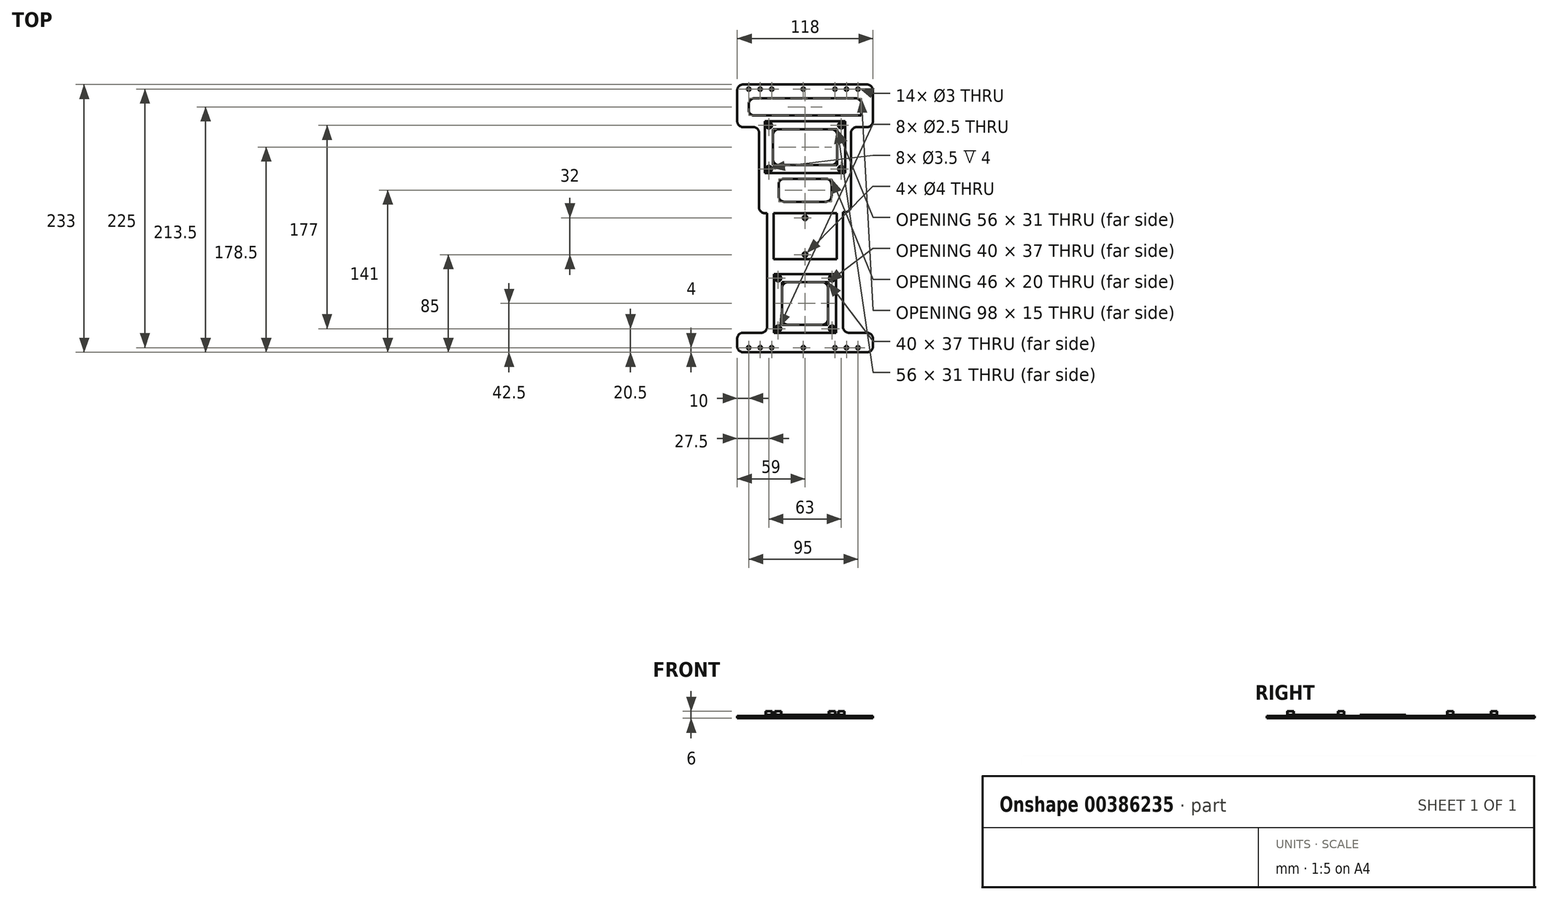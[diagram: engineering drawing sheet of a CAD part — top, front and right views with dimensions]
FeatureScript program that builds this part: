
annotation { "Feature Type Name" : "Feature", "Feature Type Description" : "" }
export const myFeature = defineFeature(function(context is Context, id is Id, definition is map)
    precondition{}
    {
        {
            var Q0;
            Q0=qCreatedBy(makeId("Top.planeOp"),FACE);
            var sketch = newSketch(context, id + "F0", { "sketchPlane" : qUnion([Q0])});
            skLineSegment(sketch, "E0.bottom", {"start": v(-25.5, -34.75) * mm, "end": v(28.5, -34.75) * mm});
            skLineSegment(sketch, "E0.top", {"start": v(-25.5, -85.75) * mm, "end": v(28.5, -85.75) * mm});
            skLineSegment(sketch, "E0.left", {"start": v(-25.5, -34.75) * mm, "end": v(-25.5, -85.75) * mm});
            skLineSegment(sketch, "E0.right", {"start": v(28.5, -34.75) * mm, "end": v(28.5, -85.75) * mm});
            skCircle(sketch, "E1", {"center": v(-22, -38.25) * mm, "radius": 1.75 * mm});
            skCircle(sketch, "E2", {"center": v(-22, -82.25) * mm, "radius": 1.75 * mm});
            skCircle(sketch, "E3", {"center": v(25, -82.25) * mm, "radius": 1.75 * mm});
            skCircle(sketch, "E4", {"center": v(25, -38.25) * mm, "radius": 1.75 * mm});
            skLineSegment(sketch, "E5.bottom", {"start": v(-18.5, -78.75) * mm, "end": v(21.5, -78.75) * mm});
            skLineSegment(sketch, "E5.top", {"start": v(-18.5, -41.75) * mm, "end": v(21.5, -41.75) * mm});
            skLineSegment(sketch, "E5.left", {"start": v(-18.5, -78.75) * mm, "end": v(-18.5, -41.75) * mm});
            skLineSegment(sketch, "E5.right", {"start": v(21.5, -78.75) * mm, "end": v(21.5, -41.75) * mm});
            skCircle(sketch, "E6", {"center": v(-22, -38.25) * mm, "radius": 2.75 * mm});
            skCircle(sketch, "E7", {"center": v(-22, -82.25) * mm, "radius": 2.75 * mm});
            skCircle(sketch, "E8", {"center": v(25, -82.25) * mm, "radius": 2.75 * mm});
            skCircle(sketch, "E9", {"center": v(25, -38.25) * mm, "radius": 2.75 * mm});
            skSolve(sketch);
        }
        {
            var Q0;
            Q0=makeQuery(id+"F0.imprint","IMPRINT",FACE,{"disambiguationData":[TD([[makeQuery(id+"F0.imprint","IMPRINT",EDGE,{"derivedFrom":sQuery(id+"F0.wireOp",EDGE,"E0.bottom")}),-1.0]])]});
            extrude(context, id + "F1", {"entities" : qUnion([Q0]), "depth" : 1 * mm});
        }
        {
            var Q0;
            Q0=makeQuery(id+"F0.imprint","IMPRINT",FACE,{"disambiguationData":[TD([[makeQuery(id+"F0.imprint","IMPRINT",EDGE,{"derivedFrom":sQuery(id+"F0.wireOp",EDGE,"E1")}),-1.0]])]});
            var Q1;
            Q1=makeQuery(id+"F0.imprint","IMPRINT",FACE,{"disambiguationData":[TD([[makeQuery(id+"F0.imprint","IMPRINT",EDGE,{"derivedFrom":sQuery(id+"F0.wireOp",EDGE,"E4")}),-1.0]])]});
            var Q2;
            Q2=makeQuery(id+"F0.imprint","IMPRINT",FACE,{"disambiguationData":[TD([[makeQuery(id+"F0.imprint","IMPRINT",EDGE,{"derivedFrom":sQuery(id+"F0.wireOp",EDGE,"E3")}),-1.0]])]});
            var Q3;
            Q3=makeQuery(id+"F0.imprint","IMPRINT",FACE,{"disambiguationData":[TD([[makeQuery(id+"F0.imprint","IMPRINT",EDGE,{"derivedFrom":sQuery(id+"F0.wireOp",EDGE,"E2")}),-1.0]])]});
            extrude(context, id + "F2", {"entities" : qUnion([Q0, Q1, Q2, Q3]), "operationType" : NewBodyOperationType.ADD, "depth" : 4 * mm});
        }
        {
            var Q0;
            Q0=qCreatedBy(makeId("Top.planeOp"),FACE);
            var sketch = newSketch(context, id + "F3", { "sketchPlane" : qUnion([Q0])});
            skLineSegment(sketch, "E10.bottom", {"start": v(-26, 18.25) * mm, "end": v(29, 18.25) * mm});
            skLineSegment(sketch, "E10.top", {"start": v(-26, -21.75) * mm, "end": v(29, -21.75) * mm});
            skLineSegment(sketch, "E10.left", {"start": v(-26, 18.25) * mm, "end": v(-26, -21.75) * mm});
            skLineSegment(sketch, "E10.right", {"start": v(29, 18.25) * mm, "end": v(29, -21.75) * mm});
            skCircle(sketch, "E11", {"center": v(1.5, 14.25) * mm, "radius": 2 * mm});
            skCircle(sketch, "E12", {"center": v(1.5, -17.75) * mm, "radius": 2 * mm});
            skSolve(sketch);
        }
        {
            var Q0;
            Q0 = qSketchRegion(id + "F3", true);
            extrude(context, id + "F4", {"entities" : qUnion([Q0]), "depth" : 1 * mm});
        }
        {
            var Q0;
            Q0=qCreatedBy(makeId("Top.planeOp"),FACE);
            var sketch = newSketch(context, id + "F5", { "sketchPlane" : qUnion([Q0])});
            skLineSegment(sketch, "E13.bottom", {"start": v(-33.5, 98.25) * mm, "end": v(36.5, 98.25) * mm});
            skLineSegment(sketch, "E13.top", {"start": v(-33.5, 53.25) * mm, "end": v(36.5, 53.25) * mm});
            skLineSegment(sketch, "E13.left", {"start": v(-33.5, 98.25) * mm, "end": v(-33.5, 53.25) * mm});
            skLineSegment(sketch, "E13.right", {"start": v(36.5, 98.25) * mm, "end": v(36.5, 53.25) * mm});
            skCircle(sketch, "E14", {"center": v(-30, 94.75) * mm, "radius": 1.75 * mm});
            skCircle(sketch, "E15", {"center": v(-30, 56.75) * mm, "radius": 1.75 * mm});
            skCircle(sketch, "E16", {"center": v(33, 56.75) * mm, "radius": 1.75 * mm});
            skCircle(sketch, "E17", {"center": v(33, 94.75) * mm, "radius": 1.75 * mm});
            skLineSegment(sketch, "E18.bottom", {"start": v(-26.5, 60.25) * mm, "end": v(29.5, 60.25) * mm});
            skLineSegment(sketch, "E18.top", {"start": v(-26.5, 91.25) * mm, "end": v(29.5, 91.25) * mm});
            skLineSegment(sketch, "E18.left", {"start": v(-26.5, 60.25) * mm, "end": v(-26.5, 91.25) * mm});
            skLineSegment(sketch, "E18.right", {"start": v(29.5, 60.25) * mm, "end": v(29.5, 91.25) * mm});
            skCircle(sketch, "E19", {"center": v(-30, 94.75) * mm, "radius": 2.75 * mm});
            skCircle(sketch, "E20", {"center": v(-30, 56.75) * mm, "radius": 2.75 * mm});
            skCircle(sketch, "E21", {"center": v(33, 56.75) * mm, "radius": 2.75 * mm});
            skCircle(sketch, "E22", {"center": v(33, 94.75) * mm, "radius": 2.75 * mm});
            skSolve(sketch);
        }
        {
            var Q0;
            Q0=makeQuery(id+"F5.imprint","IMPRINT",FACE,{"disambiguationData":[TD([[makeQuery(id+"F5.imprint","IMPRINT",EDGE,{"derivedFrom":sQuery(id+"F5.wireOp",EDGE,"E13.bottom")}),-1.0]])]});
            extrude(context, id + "F6", {"entities" : qUnion([Q0]), "depth" : 1 * mm});
        }
        {
            var Q0;
            Q0=makeQuery(id+"F5.imprint","IMPRINT",FACE,{"disambiguationData":[TD([[makeQuery(id+"F5.imprint","IMPRINT",EDGE,{"derivedFrom":sQuery(id+"F5.wireOp",EDGE,"E14")}),-1.0]])]});
            var Q1;
            Q1=makeQuery(id+"F5.imprint","IMPRINT",FACE,{"disambiguationData":[TD([[makeQuery(id+"F5.imprint","IMPRINT",EDGE,{"derivedFrom":sQuery(id+"F5.wireOp",EDGE,"E17")}),-1.0]])]});
            var Q2;
            Q2=makeQuery(id+"F5.imprint","IMPRINT",FACE,{"disambiguationData":[TD([[makeQuery(id+"F5.imprint","IMPRINT",EDGE,{"derivedFrom":sQuery(id+"F5.wireOp",EDGE,"E15")}),-1.0]])]});
            var Q3;
            Q3=makeQuery(id+"F5.imprint","IMPRINT",FACE,{"disambiguationData":[TD([[makeQuery(id+"F5.imprint","IMPRINT",EDGE,{"derivedFrom":sQuery(id+"F5.wireOp",EDGE,"E16")}),-1.0]])]});
            extrude(context, id + "F7", {"entities" : qUnion([Q0, Q1, Q2, Q3]), "operationType" : NewBodyOperationType.ADD, "depth" : 4 * mm});
        }
        {
            var Q0;
            Q0=qCreatedBy(makeId("Top.planeOp"),FACE);
            var sketch = newSketch(context, id + "F8", { "sketchPlane" : qUnion([Q0])});
            skLineSegment(sketch, "E23.bottom", {"start": v(60.5, 130.25) * mm, "end": v(-57.5, 130.25) * mm});
            skLineSegment(sketch, "E23.top", {"start": v(60.5, -102.75) * mm, "end": v(-57.5, -102.75) * mm});
            skLineSegment(sketch, "E23.left", {"start": v(60.5, 130.25) * mm, "end": v(60.5, -102.75) * mm});
            skLineSegment(sketch, "E23.right", {"start": v(-57.5, 130.25) * mm, "end": v(-57.5, -102.75) * mm});
            skPoint(sketch, "E23.middle", {"position": v(1.5, 13.75) * mm});
            skLineSegment(sketch, "E24.bottom", {"start": v(-26.5, 91.25) * mm, "end": v(29.5, 91.25) * mm});
            skLineSegment(sketch, "E24.top", {"start": v(-26.5, 60.25) * mm, "end": v(29.5, 60.25) * mm});
            skLineSegment(sketch, "E24.left", {"start": v(-26.5, 91.25) * mm, "end": v(-26.5, 60.25) * mm});
            skLineSegment(sketch, "E24.right", {"start": v(29.5, 91.25) * mm, "end": v(29.5, 60.25) * mm});
            skLineSegment(sketch, "E25.right", {"start": v(55.5, -92.75) * mm, "end": v(55.5, -90.75) * mm});
            skLineSegment(sketch, "E26.bottom", {"start": v(34.5, -85.75) * mm, "end": v(60.5, -85.75) * mm});
            skLineSegment(sketch, "E26.top", {"start": v(34.5, 19.25) * mm, "end": v(60.5, 19.25) * mm});
            skLineSegment(sketch, "E26.left", {"start": v(34.5, -85.75) * mm, "end": v(34.5, 19.25) * mm});
            skLineSegment(sketch, "E26.right", {"start": v(60.5, -85.75) * mm, "end": v(60.5, 19.25) * mm});
            skLineSegment(sketch, "E27.bottom", {"start": v(-57.5, -85.75) * mm, "end": v(-31.5, -85.75) * mm});
            skLineSegment(sketch, "E27.top", {"start": v(-57.5, 18.25) * mm, "end": v(-31.5, 18.25) * mm});
            skLineSegment(sketch, "E27.left", {"start": v(-57.5, -85.75) * mm, "end": v(-57.5, 18.25) * mm});
            skLineSegment(sketch, "E27.right", {"start": v(-31.5, -85.75) * mm, "end": v(-31.5, 18.25) * mm});
            skCircle(sketch, "E28", {"center": v(0, -98.75) * mm, "radius": 1.5 * mm});
            skCircle(sketch, "E29", {"center": v(37.5, -98.75) * mm, "radius": 1.5 * mm});
            skCircle(sketch, "E30", {"center": v(-37.5, -98.75) * mm, "radius": 1.5 * mm});
            skCircle(sketch, "E31", {"center": v(0, 126.25) * mm, "radius": 1.5 * mm});
            skCircle(sketch, "E32", {"center": v(37.5, 126.25) * mm, "radius": 1.5 * mm});
            skCircle(sketch, "E33", {"center": v(-37.5, 126.25) * mm, "radius": 1.5 * mm});
            skLineSegment(sketch, "E34.bottom", {"start": v(-18.5, -41.75) * mm, "end": v(21.5, -41.75) * mm});
            skLineSegment(sketch, "E34.top", {"start": v(-18.5, -78.75) * mm, "end": v(21.5, -78.75) * mm});
            skLineSegment(sketch, "E34.left", {"start": v(-18.5, -41.75) * mm, "end": v(-18.5, -78.75) * mm});
            skLineSegment(sketch, "E34.right", {"start": v(21.5, -41.75) * mm, "end": v(21.5, -78.75) * mm});
            skCircle(sketch, "E35", {"center": v(1.5, -17.75) * mm, "radius": 2 * mm});
            skCircle(sketch, "E36", {"center": v(1.5, 14.25) * mm, "radius": 2 * mm});
            skCircle(sketch, "E37", {"center": v(-47.5, -98.75) * mm, "radius": 1.5 * mm});
            skCircle(sketch, "E38", {"center": v(-27.5, -98.75) * mm, "radius": 1.5 * mm});
            skCircle(sketch, "E39", {"center": v(27.5, -98.75) * mm, "radius": 1.5 * mm});
            skCircle(sketch, "E40", {"center": v(47.5, -98.75) * mm, "radius": 1.5 * mm});
            skCircle(sketch, "E41", {"center": v(-47.5, 126.25) * mm, "radius": 1.5 * mm});
            skCircle(sketch, "E42", {"center": v(-27.5, 126.25) * mm, "radius": 1.5 * mm});
            skCircle(sketch, "E43", {"center": v(27.5, 126.25) * mm, "radius": 1.5 * mm});
            skCircle(sketch, "E44", {"center": v(47.5, 126.25) * mm, "radius": 1.5 * mm});
            skLineSegment(sketch, "E45.bottom", {"start": v(-21.5, 48.25) * mm, "end": v(24.5, 48.25) * mm});
            skLineSegment(sketch, "E45.top", {"start": v(-21.5, 28.25) * mm, "end": v(24.5, 28.25) * mm});
            skLineSegment(sketch, "E45.left", {"start": v(-21.5, 48.25) * mm, "end": v(-21.5, 28.25) * mm});
            skLineSegment(sketch, "E45.right", {"start": v(24.5, 48.25) * mm, "end": v(24.5, 28.25) * mm});
            skLineSegment(sketch, "E46.bottom", {"start": v(-47.5, 103.25) * mm, "end": v(50.5, 103.25) * mm});
            skLineSegment(sketch, "E46.top", {"start": v(-47.5, 118.25) * mm, "end": v(50.5, 118.25) * mm});
            skLineSegment(sketch, "E46.left", {"start": v(-47.5, 103.25) * mm, "end": v(-47.5, 118.25) * mm});
            skLineSegment(sketch, "E46.right", {"start": v(50.5, 103.25) * mm, "end": v(50.5, 118.25) * mm});
            skCircle(sketch, "E47", {"center": v(-22, -82.25) * mm, "radius": 1.25 * mm});
            skCircle(sketch, "E48", {"center": v(25, -82.25) * mm, "radius": 1.25 * mm});
            skCircle(sketch, "E49", {"center": v(25, -38.25) * mm, "radius": 1.25 * mm});
            skCircle(sketch, "E50", {"center": v(-22, -38.25) * mm, "radius": 1.25 * mm});
            skCircle(sketch, "E51", {"center": v(-30, 56.75) * mm, "radius": 1.25 * mm});
            skCircle(sketch, "E52", {"center": v(33, 56.75) * mm, "radius": 1.25 * mm});
            skCircle(sketch, "E53", {"center": v(33, 94.75) * mm, "radius": 1.25 * mm});
            skCircle(sketch, "E54", {"center": v(-30, 94.75) * mm, "radius": 1.25 * mm});
            skLineSegment(sketch, "E55", {"start": v(60.5, 93.25) * mm, "end": v(41.5, 93.25) * mm});
            skLineSegment(sketch, "E56", {"start": v(41.5, 93.25) * mm, "end": v(41.5, 19.25) * mm});
            skLineSegment(sketch, "E57", {"start": v(-57.5, 93.25) * mm, "end": v(-38.5, 93.25) * mm});
            skLineSegment(sketch, "E58", {"start": v(-38.5, 93.25) * mm, "end": v(-38.5, 18.25) * mm});
            skSolve(sketch);
        }
        {
            var Q0;
            Q0=makeQuery(id+"F8.imprint","IMPRINT",FACE,{"disambiguationData":[TD([[makeQuery(id+"F8.imprint","IMPRINT",EDGE,{"derivedFrom":sQuery(id+"F8.wireOp",EDGE,"E23.bottom")}),1.0]])]});
            extrude(context, id + "F9", {"entities" : qUnion([Q0]), "oppositeDirection" : true, "depth" : 2 * mm});
        }
        {
            var Q0;
            Q0=makeQuery(id+"F9.opExtrude","SWEPT_EDGE",EDGE,{"disambiguationData":[OSD([sQuery(id+"F8.wireOp",EDGE,"E26.top"),sQuery(id+"F8.wireOp",EDGE,"E56")])]});
            var Q1;
            Q1=makeQuery(id+"F9.opExtrude","SWEPT_EDGE",EDGE,{"disambiguationData":[OSD([sQuery(id+"F8.wireOp",EDGE,"E23.top"),sQuery(id+"F8.wireOp",EDGE,"E23.left")])]});
            var Q2;
            Q2=makeQuery(id+"F9.opExtrude","SWEPT_EDGE",EDGE,{"disambiguationData":[OSD([sQuery(id+"F8.wireOp",EDGE,"E23.top"),sQuery(id+"F8.wireOp",EDGE,"E23.right")])]});
            var Q3;
            Q3=makeQuery(id+"F9.opExtrude","SWEPT_EDGE",EDGE,{"disambiguationData":[OSD([sQuery(id+"F8.wireOp",EDGE,"E23.bottom"),sQuery(id+"F8.wireOp",EDGE,"E23.left")])]});
            var Q4;
            Q4=makeQuery(id+"F9.opExtrude","SWEPT_EDGE",EDGE,{"disambiguationData":[OSD([sQuery(id+"F8.wireOp",EDGE,"E23.bottom"),sQuery(id+"F8.wireOp",EDGE,"E23.right")])]});
            var Q5;
            Q5=makeQuery(id+"F9.opExtrude","SWEPT_EDGE",EDGE,{"disambiguationData":[OSD([sQuery(id+"F8.wireOp",EDGE,"E24.top"),sQuery(id+"F8.wireOp",EDGE,"E24.left")])]});
            var Q6;
            Q6=makeQuery(id+"F9.opExtrude","SWEPT_EDGE",EDGE,{"disambiguationData":[OSD([sQuery(id+"F8.wireOp",EDGE,"E24.bottom"),sQuery(id+"F8.wireOp",EDGE,"E24.left")])]});
            var Q7;
            Q7=makeQuery(id+"F9.opExtrude","SWEPT_EDGE",EDGE,{"disambiguationData":[OSD([sQuery(id+"F8.wireOp",EDGE,"E24.bottom"),sQuery(id+"F8.wireOp",EDGE,"E24.right")])]});
            var Q8;
            Q8=makeQuery(id+"F9.opExtrude","SWEPT_EDGE",EDGE,{"disambiguationData":[OSD([sQuery(id+"F8.wireOp",EDGE,"E24.top"),sQuery(id+"F8.wireOp",EDGE,"E24.right")])]});
            var Q9;
            Q9=makeQuery(id+"F9.opExtrude","SWEPT_EDGE",EDGE,{"disambiguationData":[OSD([sQuery(id+"F8.wireOp",EDGE,"E23.right"),sQuery(id+"F8.wireOp",EDGE,"E27.bottom"),sQuery(id+"F8.wireOp",EDGE,"E27.left")])]});
            var Q10;
            Q10=makeQuery(id+"F9.opExtrude","SWEPT_EDGE",EDGE,{"disambiguationData":[OSD([sQuery(id+"F8.wireOp",EDGE,"E26.bottom"),sQuery(id+"F8.wireOp",EDGE,"E26.left")])]});
            var Q11;
            Q11=makeQuery(id+"F9.opExtrude","SWEPT_EDGE",EDGE,{"disambiguationData":[OSD([sQuery(id+"F8.wireOp",EDGE,"E23.left"),sQuery(id+"F8.wireOp",EDGE,"E26.bottom"),sQuery(id+"F8.wireOp",EDGE,"E26.right")])]});
            var Q12;
            Q12=makeQuery(id+"F9.opExtrude","SWEPT_EDGE",EDGE,{"disambiguationData":[OSD([sQuery(id+"F8.wireOp",EDGE,"E27.bottom"),sQuery(id+"F8.wireOp",EDGE,"E27.right")])]});
            var Q13;
            Q13=makeQuery(id+"F9.opExtrude","SWEPT_EDGE",EDGE,{"disambiguationData":[OSD([sQuery(id+"F8.wireOp",EDGE,"E34.top"),sQuery(id+"F8.wireOp",EDGE,"E34.left")])]});
            var Q14;
            Q14=makeQuery(id+"F9.opExtrude","SWEPT_EDGE",EDGE,{"disambiguationData":[OSD([sQuery(id+"F8.wireOp",EDGE,"E34.top"),sQuery(id+"F8.wireOp",EDGE,"E34.right")])]});
            var Q15;
            Q15=makeQuery(id+"F9.opExtrude","SWEPT_EDGE",EDGE,{"disambiguationData":[OSD([sQuery(id+"F8.wireOp",EDGE,"E34.bottom"),sQuery(id+"F8.wireOp",EDGE,"E34.left")])]});
            var Q16;
            Q16=makeQuery(id+"F9.opExtrude","SWEPT_EDGE",EDGE,{"disambiguationData":[OSD([sQuery(id+"F8.wireOp",EDGE,"E34.bottom"),sQuery(id+"F8.wireOp",EDGE,"E34.right")])]});
            var Q17;
            Q17=makeQuery(id+"F9.opExtrude","SWEPT_EDGE",EDGE,{"disambiguationData":[OSD([sQuery(id+"F8.wireOp",EDGE,"E46.top"),sQuery(id+"F8.wireOp",EDGE,"E46.right")])]});
            var Q18;
            Q18=makeQuery(id+"F9.opExtrude","SWEPT_EDGE",EDGE,{"disambiguationData":[OSD([sQuery(id+"F8.wireOp",EDGE,"E45.bottom"),sQuery(id+"F8.wireOp",EDGE,"E45.right")])]});
            var Q19;
            Q19=makeQuery(id+"F9.opExtrude","SWEPT_EDGE",EDGE,{"disambiguationData":[OSD([sQuery(id+"F8.wireOp",EDGE,"E46.top"),sQuery(id+"F8.wireOp",EDGE,"E46.left")])]});
            var Q20;
            Q20=makeQuery(id+"F9.opExtrude","SWEPT_EDGE",EDGE,{"disambiguationData":[OSD([sQuery(id+"F8.wireOp",EDGE,"E45.bottom"),sQuery(id+"F8.wireOp",EDGE,"E45.left")])]});
            var Q21;
            Q21=makeQuery(id+"F9.opExtrude","SWEPT_EDGE",EDGE,{"disambiguationData":[OSD([sQuery(id+"F8.wireOp",EDGE,"E45.top"),sQuery(id+"F8.wireOp",EDGE,"E45.left")])]});
            var Q22;
            Q22=makeQuery(id+"F9.opExtrude","SWEPT_EDGE",EDGE,{"disambiguationData":[OSD([sQuery(id+"F8.wireOp",EDGE,"E46.bottom"),sQuery(id+"F8.wireOp",EDGE,"E46.left")])]});
            var Q23;
            Q23=makeQuery(id+"F9.opExtrude","SWEPT_EDGE",EDGE,{"disambiguationData":[OSD([sQuery(id+"F8.wireOp",EDGE,"E45.top"),sQuery(id+"F8.wireOp",EDGE,"E45.right")])]});
            var Q24;
            Q24=makeQuery(id+"F9.opExtrude","SWEPT_EDGE",EDGE,{"disambiguationData":[OSD([sQuery(id+"F8.wireOp",EDGE,"E23.right"),sQuery(id+"F8.wireOp",EDGE,"E57")])]});
            var Q25;
            Q25=makeQuery(id+"F9.opExtrude","SWEPT_EDGE",EDGE,{"disambiguationData":[OSD([sQuery(id+"F8.wireOp",EDGE,"E57"),sQuery(id+"F8.wireOp",EDGE,"E58")])]});
            var Q26;
            Q26=makeQuery(id+"F9.opExtrude","SWEPT_EDGE",EDGE,{"disambiguationData":[OSD([sQuery(id+"F8.wireOp",EDGE,"E23.left"),sQuery(id+"F8.wireOp",EDGE,"E55")])]});
            var Q27;
            Q27=makeQuery(id+"F9.opExtrude","SWEPT_EDGE",EDGE,{"disambiguationData":[OSD([sQuery(id+"F8.wireOp",EDGE,"E55"),sQuery(id+"F8.wireOp",EDGE,"E56")])]});
            var Q28;
            Q28=makeQuery(id+"F9.opExtrude","SWEPT_EDGE",EDGE,{"disambiguationData":[OSD([sQuery(id+"F8.wireOp",EDGE,"E27.top"),sQuery(id+"F8.wireOp",EDGE,"E58")])]});
            fillet(context, id + "F10", {"entities" : qUnion([Q0, Q1, Q2, Q3, Q4, Q5, Q6, Q7, Q8, Q9, Q10, Q11, Q12, Q13, Q14, Q15, Q16, Q17, Q18, Q19, Q20, Q21, Q22, Q23, Q24, Q25, Q26, Q27, Q28]), "radius" : 5 * mm, "tangentPropagation" : true, "allowEdgeOverflow" : false});
        }
    });
